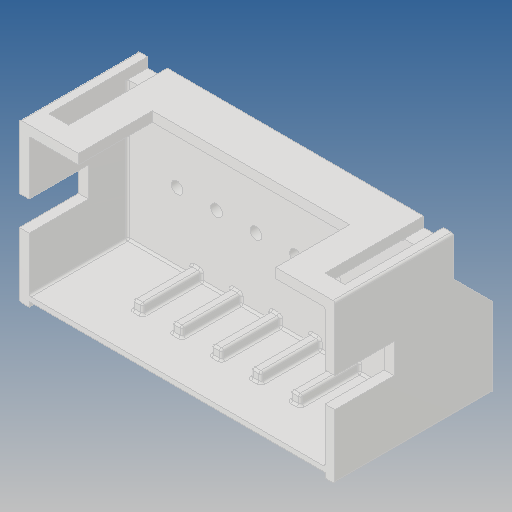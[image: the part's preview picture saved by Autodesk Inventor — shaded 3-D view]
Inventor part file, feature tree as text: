
AUTODESK INVENTOR PART (.ipt)
format: ipt  version: 2020 (Build 240168000, 168)  size: 262,144 bytes
history: mixed  units: mm
features: other x1, fillet x1, imported_body x1
ambient origin geometry x8: Origin, YZ Plane, XZ Plane, XY Plane, X Axis, Y Axis, Z Axis, Center Point
bodies: Body1 (imported_parasolid)
feature tree (3):
  other  "Твердое тело1"
  fillet  "Fillet1"  [1 undecoded]
  imported_body  NMx_Import_Brep_tag  [imported B-rep: ~180 faces, bbox_mm=[16.0, 8.0, 8.0]]
note: 1 required parameter value undecoded (feature->parameter linkage not recoverable at this tier; creation-order binding heuristic only, values carry confidence <= 0.55)
